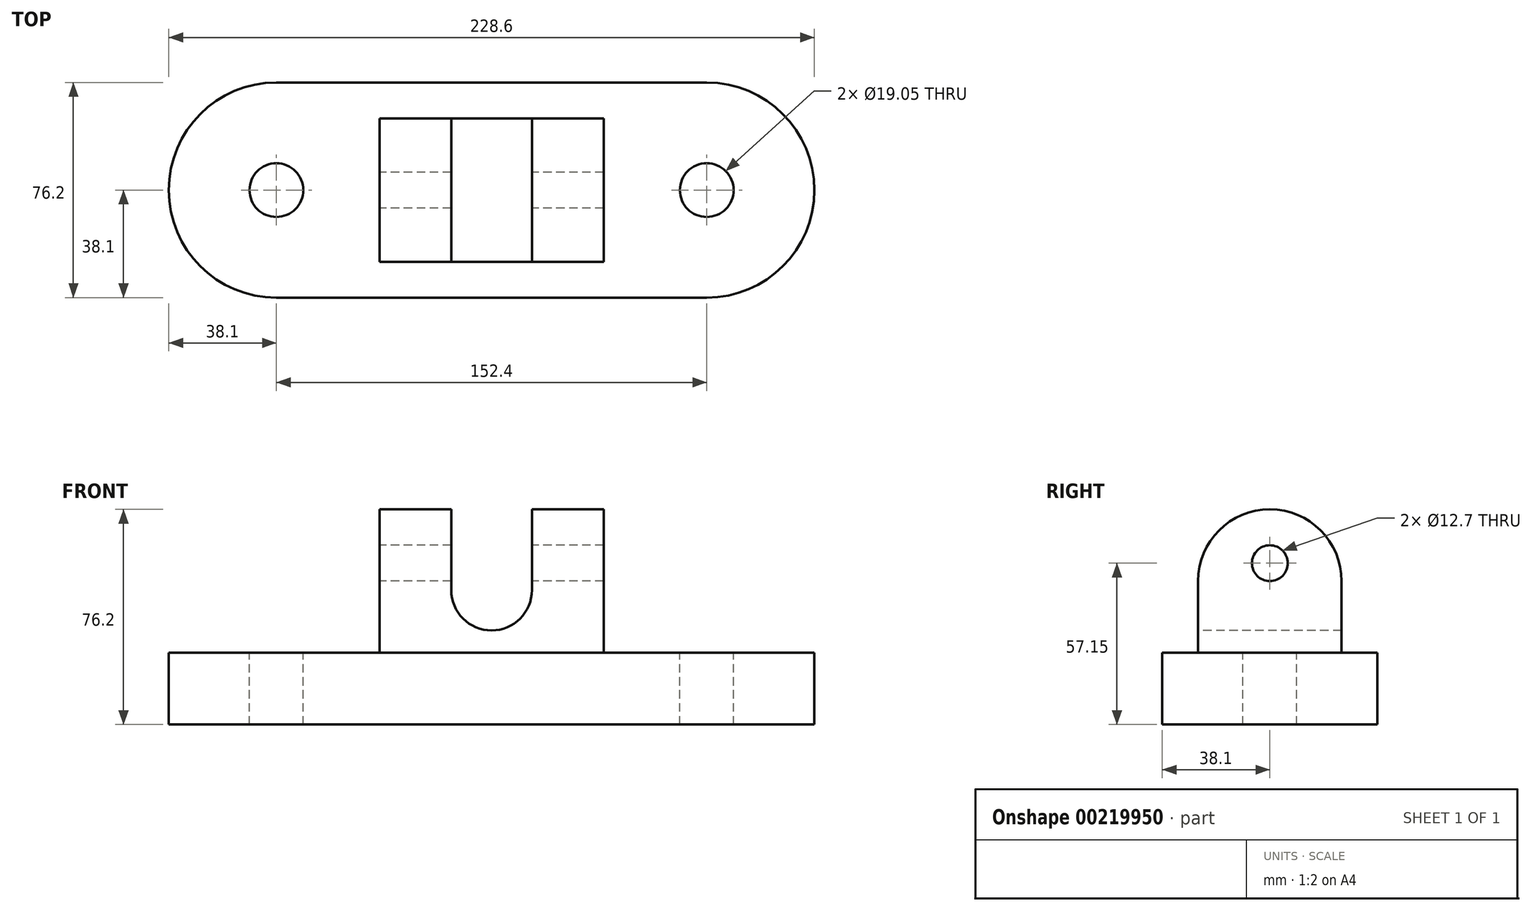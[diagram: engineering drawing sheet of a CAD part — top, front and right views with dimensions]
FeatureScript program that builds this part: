
annotation { "Feature Type Name" : "Feature", "Feature Type Description" : "" }
export const myFeature = defineFeature(function(context is Context, id is Id, definition is map)
    precondition{}
    {
        {
            var Q0;
            Q0=qCreatedBy(makeId("Top.planeOp"),FACE);
            var sketch = newSketch(context, id + "F0", { "sketchPlane" : qUnion([Q0])});
            skLineSegment(sketch, "E0.bottom", {"start": v(76.2, 38.1) * mm, "end": v(-76.2, 38.1) * mm});
            skLineSegment(sketch, "E0.top", {"start": v(76.2, -38.1) * mm, "end": v(-76.2, -38.1) * mm});
            skPoint(sketch, "E0.middle", {"position": v(0, 0) * mm});
            skArc(sketch, "E1", {"start": v(-76.2, 38.1) * mm, "mid": v(-114.3, 0) * mm, "end": v(-76.2, -38.1) * mm});
            skArc(sketch, "E2", {"start": v(76.2, -38.1) * mm, "mid": v(114.3, 0) * mm, "end": v(76.2, 38.1) * mm});
            skLineSegment(sketch, "E3", {"start": v(-76.2, -38.1) * mm, "end": v(-76.2, 38.1) * mm, "construction": true});
            skLineSegment(sketch, "E4", {"start": v(76.2, -38.1) * mm, "end": v(76.2, 38.1) * mm, "construction": true});
            skSolve(sketch);
        }
        {
            var Q0;
            Q0 = qSketchRegion(id + "F0", true);
            extrude(context, id + "F1", {"entities" : qUnion([Q0]), "depth" : 25.4 * mm});
        }
        {
            var Q0;
            Q0=makeQuery(id+"F1.opExtrude","CAP_FACE",FACE,{"disambiguationData":[OSD([sQuery(id+"F0.wireOp",EDGE,"E0.bottom"),sQuery(id+"F0.wireOp",EDGE,"E0.top"),sQuery(id+"F0.wireOp",EDGE,"E1"),sQuery(id+"F0.wireOp",EDGE,"E2")])],"isStart":false});
            var sketch = newSketch(context, id + "F2", { "sketchPlane" : qUnion([Q0])});
            skLineSegment(sketch, "E5.bottom", {"start": v(39.69, 25.4) * mm, "end": v(-39.69, 25.4) * mm});
            skLineSegment(sketch, "E5.top", {"start": v(39.69, -25.4) * mm, "end": v(-39.69, -25.4) * mm});
            skLineSegment(sketch, "E5.left", {"start": v(39.69, 25.4) * mm, "end": v(39.69, -25.4) * mm});
            skLineSegment(sketch, "E5.right", {"start": v(-39.69, 25.4) * mm, "end": v(-39.69, -25.4) * mm});
            skPoint(sketch, "E5.middle", {"position": v(0, 0) * mm});
            skSolve(sketch);
        }
        {
            var Q0;
            Q0 = qSketchRegion(id + "F2", true);
            extrude(context, id + "F3", {"entities" : qUnion([Q0]), "operationType" : NewBodyOperationType.ADD, "depth" : 50.8 * mm});
        }
        {
            var Q0;
            Q0=makeQuery(id+"F3.opExtrude","SWEPT_FACE",FACE,{"disambiguationData":[OSD([sQuery(id+"F2.wireOp",EDGE,"E5.top")])]});
            var sketch = newSketch(context, id + "F4", { "sketchPlane" : qUnion([Q0])});
            skLineSegment(sketch, "E6", {"start": v(-14.29, 76.2) * mm, "end": v(-14.29, 47.62) * mm});
            skLineSegment(sketch, "E7", {"start": v(-14.29, 47.62) * mm, "end": v(14.29, 47.63) * mm, "construction": true});
            skLineSegment(sketch, "E8", {"start": v(14.29, 47.63) * mm, "end": v(14.29, 76.2) * mm});
            skLineSegment(sketch, "E9", {"start": v(14.29, 76.2) * mm, "end": v(-14.29, 76.2) * mm});
            skLineSegment(sketch, "E10", {"start": v(0, 25.4) * mm, "end": v(0, 76.2) * mm, "construction": true});
            skArc(sketch, "E11", {"start": v(-14.29, 47.62) * mm, "mid": v(0, 33.34) * mm, "end": v(14.29, 47.63) * mm});
            skSolve(sketch);
        }
        {
            var Q0;
            Q0 = qSketchRegion(id + "F4", true);
            var Q1;
            Q1 = qConstructionFilter(qBodyType(qCreatedBy(id + "F4" ,EDGE), BodyType.WIRE), ConstructionObject.NO);
            extrude(context, id + "F5", {"entities" : qUnion([Q0]), "operationType" : NewBodyOperationType.REMOVE, "surfaceEntities" : qUnion([Q1]), "endBound" : BoundingType.THROUGH_ALL, "oppositeDirection" : true, "depth" : 25.4 * mm});
        }
        {
            var Q0;
            {var subQ0=sQuery(id+"F2.wireOp",EDGE,"E5.right");var subQ1=sQuery(id+"F2.wireOp",EDGE,"E5.top");Q0=makeQuery(id+"F5.boolean.opBoolean","SPLIT",EDGE,{"disambiguationData":[TD([makeQuery(id+"F3.opExtrude","SWEPT_FACE",FACE,{"disambiguationData":[OSD([subQ0])]})])],"derivedFrom":makeQuery(id+"F3.opExtrude","CAP_EDGE",EDGE,{"disambiguationData":[OSD([subQ1])],"isStart":false})});}
            var Q1;
            {var subQ0=sQuery(id+"F2.wireOp",EDGE,"E5.bottom");var subQ1=sQuery(id+"F2.wireOp",EDGE,"E5.right");Q1=makeQuery(id+"F5.boolean.opBoolean","SPLIT",EDGE,{"disambiguationData":[TD([makeQuery(id+"F3.opExtrude","SWEPT_FACE",FACE,{"disambiguationData":[OSD([subQ1])]})])],"derivedFrom":makeQuery(id+"F3.opExtrude","CAP_EDGE",EDGE,{"disambiguationData":[OSD([subQ0])],"isStart":false})});}
            var Q2;
            {var subQ0=sQuery(id+"F2.wireOp",EDGE,"E5.left");var subQ1=sQuery(id+"F2.wireOp",EDGE,"E5.top");Q2=makeQuery(id+"F5.boolean.opBoolean","SPLIT",EDGE,{"disambiguationData":[TD([makeQuery(id+"F3.opExtrude","SWEPT_FACE",FACE,{"disambiguationData":[OSD([subQ0])]})])],"derivedFrom":makeQuery(id+"F3.opExtrude","CAP_EDGE",EDGE,{"disambiguationData":[OSD([subQ1])],"isStart":false})});}
            var Q3;
            {var subQ0=sQuery(id+"F2.wireOp",EDGE,"E5.bottom");var subQ1=sQuery(id+"F2.wireOp",EDGE,"E5.left");Q3=makeQuery(id+"F5.boolean.opBoolean","SPLIT",EDGE,{"disambiguationData":[TD([makeQuery(id+"F3.opExtrude","SWEPT_FACE",FACE,{"disambiguationData":[OSD([subQ1])]})])],"derivedFrom":makeQuery(id+"F3.opExtrude","CAP_EDGE",EDGE,{"disambiguationData":[OSD([subQ0])],"isStart":false})});}
            fillet(context, id + "F6", {"entities" : qUnion([Q0, Q1, Q2, Q3]), "radius" : 25.4 * mm, "tangentPropagation" : true, "allowEdgeOverflow" : false});
        }
        {
            var Q0;
            Q0=makeQuery(id+"F3.opExtrude","SWEPT_FACE",FACE,{"disambiguationData":[OSD([sQuery(id+"F2.wireOp",EDGE,"E5.right")])]});
            var sketch = newSketch(context, id + "F7", { "sketchPlane" : qUnion([Q0])});
            skCircle(sketch, "E12", {"center": v(0, 57.15) * mm, "radius": 6.35 * mm});
            skSolve(sketch);
        }
        {
            var Q0;
            Q0 = qSketchRegion(id + "F7", true);
            extrude(context, id + "F8", {"entities" : qUnion([Q0]), "operationType" : NewBodyOperationType.REMOVE, "oppositeDirection" : true, "depth" : 127 * mm});
        }
        {
            var Q0;
            Q0=makeQuery(id+"F1.opExtrude","CAP_FACE",FACE,{"disambiguationData":[OSD([sQuery(id+"F0.wireOp",EDGE,"E0.bottom"),sQuery(id+"F0.wireOp",EDGE,"E0.top"),sQuery(id+"F0.wireOp",EDGE,"E1"),sQuery(id+"F0.wireOp",EDGE,"E2")])],"isStart":false});
            var sketch = newSketch(context, id + "F9", { "sketchPlane" : qUnion([Q0])});
            skCircle(sketch, "E13", {"center": v(-76.2, 0) * mm, "radius": 9.53 * mm});
            skCircle(sketch, "E14", {"center": v(76.2, 0) * mm, "radius": 9.53 * mm});
            skSolve(sketch);
        }
        {
            var Q0;
            Q0 = qSketchRegion(id + "F9", true);
            extrude(context, id + "F10", {"entities" : qUnion([Q0]), "operationType" : NewBodyOperationType.REMOVE, "endBound" : BoundingType.THROUGH_ALL, "oppositeDirection" : true, "depth" : 25.4 * mm});
        }
    });
